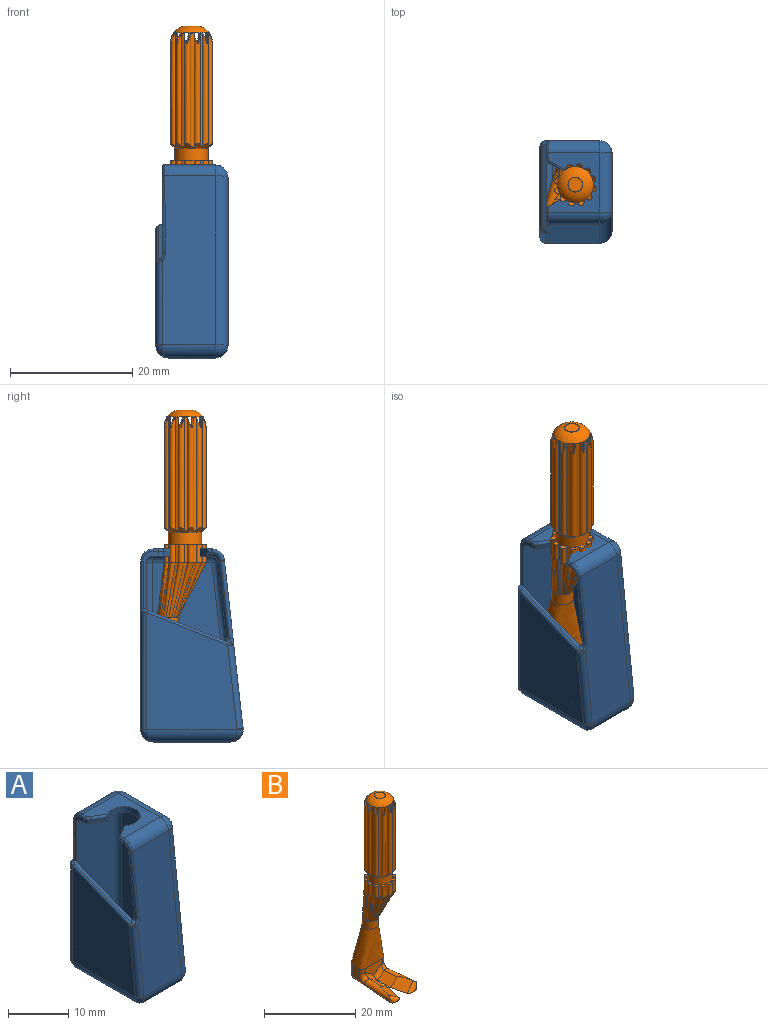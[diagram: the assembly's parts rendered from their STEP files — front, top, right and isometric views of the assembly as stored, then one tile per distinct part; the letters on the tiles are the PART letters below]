
ASSEMBLY  parts=2 mates=1
PART A: 136 faces, bbox 12x17.1x37.6 mm
  f0: plane 12.76x7.8mm, normal (0,0,-1), area 78.4mm2, adj f23,f27,f28,f29,f74,f75,f76,f77
  f1: plane 9.68x8.4mm, normal (0,0,1), area 45.1mm2, adj f14,f15,f17,f18,f19,f55,f56,f57
  f2: plane 9.71x8.6mm, normal (0,0,-1), area 44.8mm2, adj f3,f14,f15,f16,f41,f45,f48,f50
  f3: plane 9.56x2.48mm, normal (-1,0,0), area 5.7mm2, adj f2,f7,f12,f41,f51,f57,f58,f59
  f4: plane 27.72x8.92mm, normal (0,-0.99,0.11), area 237.7mm2, adj f17,f22,f27,f30,f66,f67,f68,f70
  f5: plane 12.87x7.6mm, normal (0,0,1), area 97.8mm2, adj f35,f36,f38,f39
  f6: plane 27.15x8.75mm, normal (0,0.99,-0.12), area 221mm2, adj f11,f38,f44,f47,f48,f52
  f7: plane 27x8.6mm, normal (0,-1,0), area 232.2mm2, adj f3,f11,f35,f40,f41
  f8: plane 27.6x8.8mm, normal (0,1,0), area 239.6mm2, adj f19,f24,f28,f33,f59,f60
  f9: plane 27x12.87mm, normal (-1,0,0), area 304.8mm2, adj f39,f40,f44,f45
  f10: plane 27.6x12.76mm, normal (1,0,0), area 309.6mm2, adj f18,f22,f23,f24
  f11: plane 19.27x14.89mm, normal (1,0,0), area 231.2mm2, adj f6,f7,f12,f36,f38,f52
  f12: plane 14.18x5.68mm, normal (0,-0.37,0.93), area 8.7mm2, adj f3,f11,f52,f61,f62,f63
  f13: plane 19.17x14.76mm, normal (-1,0,0), area 229.1mm2, adj f29,f30,f31,f33,f62
  f14: cylinder r=2.7mm len=5.4mm, axis (0,0,1), area 14.3mm2, adj f1,f2,f54,f55,f73
  f15: plane 2.88x1.8mm, normal (-0.52,0.86,0), area 3.5mm2, adj f1,f2,f50,f69,f73
  f16: plane 2.26x1.36mm, normal (-0.52,-0.86,0), area 2.1mm2, adj f2,f51,f54,f55
  f17: cylinder r=2mm len=8.37mm, axis (-1,0,0), area 24.4mm2, adj f1,f4,f20,f72
  f18: cylinder r=2mm len=9.68mm, axis (0,1,0), area 30.4mm2, adj f1,f10,f20,f21
  f19: cylinder r=2mm len=8.4mm, axis (1,0,0), area 26.4mm2, adj f1,f8,f21,f58
  f20: sphere r=2mm, area 5.8mm2, adj f17,f18,f22
  f21: sphere r=2mm, area 6.3mm2, adj f18,f19,f24
  f22: cylinder r=2mm len=27.82mm, axis (0,0.11,0.99), area 87.2mm2, adj f4,f10,f20,f25
  f23: cylinder r=2mm len=12.76mm, axis (0,-1,0), area 40.1mm2, adj f0,f10,f25,f26
  f24: cylinder r=2mm len=27.6mm, axis (0,0,-1), area 86.7mm2, adj f8,f10,f21,f26
  f25: sphere r=2mm, area 6.7mm2, adj f22,f23,f27
  f26: sphere r=2mm, area 6.3mm2, adj f23,f24,f28
  f27: cylinder r=2mm len=8.8mm, axis (1,0,0), area 28.5mm2, adj f0,f4,f25,f31,f32
  f28: cylinder r=2mm len=8.8mm, axis (-1,0,0), area 26.1mm2, adj f0,f8,f26,f34
  f29: cylinder r=2mm len=14.76mm, axis (0,-1,0), area 43.2mm2, adj f0,f13,f32,f34
  f30: cylinder r=1mm len=13.87mm, axis (0,0.11,0.99), area 21.5mm2, adj f4,f13,f31,f63,f64,f65
  f31: torus R=1mm, axis (-1,0,0), area 0.3mm2, adj f13,f27,f30,f32
  f32: bspline ~2.1x2mm, area 2.2mm2, adj f27,f29,f31
  f33: cylinder r=1mm len=19.41mm, axis (0,0,-1), area 30.3mm2, adj f8,f13,f34,f61
  f34: bspline ~2.39x2mm, area 2.2mm2, adj f28,f29,f33
  f35: cylinder r=1mm len=8.6mm, axis (1,0,0), area 12.7mm2, adj f5,f7,f36,f37
  f36: cylinder r=1mm len=14.87mm, axis (0,1,0), area 21.8mm2, adj f5,f11,f35,f38
  f37: sphere r=1mm, area 1mm2, adj f35,f39,f40
  f38: cylinder r=1mm len=8.6mm, axis (1,0,0), area 13.9mm2, adj f5,f6,f11,f36,f42
  f39: cylinder r=1mm len=12.87mm, axis (0,1,0), area 20.2mm2, adj f5,f9,f37,f42
  f40: cylinder r=1mm len=27mm, axis (0,0,1), area 42.4mm2, adj f7,f9,f37,f43
  f41: cylinder r=1mm len=8.6mm, axis (-1,0,0), area 13.5mm2, adj f2,f3,f7,f43
  f42: sphere r=1mm, area 1.7mm2, adj f38,f39,f44
  f43: sphere r=1mm, area 1mm2, adj f40,f41,f45
  f44: cylinder r=1mm len=27.12mm, axis (0,-0.12,-0.99), area 42.7mm2, adj f6,f9,f42,f46
  f45: cylinder r=1mm len=9.71mm, axis (0,-1,0), area 15.3mm2, adj f2,f9,f43,f46
  f46: sphere r=1mm, area 1.5mm2, adj f44,f45,f48
  f47: cylinder r=1mm len=12.74mm, axis (0,0.12,0.99), area 12.9mm2, adj f6,f49,f52,f68
  f48: cylinder r=1mm len=7.6mm, axis (-1,0,0), area 11.1mm2, adj f2,f6,f46,f49
  f49: torus R=2mm, axis (1,0,0), area 2.2mm2, adj f47,f48,f50,f70,f71,f72
  f50: cylinder r=1mm len=1.15mm, axis (0,1,0), area 1.1mm2, adj f2,f15,f49,f69
  f51: cylinder r=1mm len=0.86mm, axis (0,0,1), area 0.8mm2, adj f2,f3,f16,f56
  f52: bspline ~1.77x1.5mm, area 0.9mm2, adj f6,f11,f12,f47,f53,f64,f67
  f53: cylinder r=0.5mm len=0.15mm, axis (0,-0.93,-0.37), area 0mm2, adj f52,f65,f66
  f54: cylinder r=0.4mm len=1.17mm, axis (0,0,1), area 0.5mm2, adj f2,f14,f16,f55
  f55: cylinder r=0.4mm len=2.84mm, axis (0.86,-0.52,0), area 1.8mm2, adj f1,f14,f16,f54,f56
  f56: torus R=0.6mm, axis (0,0,1), area 0.6mm2, adj f1,f51,f55,f57
  f57: cylinder r=0.4mm len=0.87mm, axis (0,-1,0), area 0.5mm2, adj f1,f3,f56,f58
  f58: torus R=1.6mm, axis (1,0,0), area 1.8mm2, adj f3,f19,f57,f59
  f59: cylinder r=0.4mm len=8.19mm, axis (0,0,1), area 5mm2, adj f3,f8,f58,f60
  f60: cylinder r=0.4mm len=0.4mm, axis (-1,0,0), area 0.1mm2, adj f8,f59,f61
  f61: bspline ~1.15x1mm, area 1mm2, adj f3,f12,f33,f60,f62
  f62: cylinder r=0.4mm len=13.36mm, axis (0,-0.93,-0.37), area 8.9mm2, adj f12,f13,f61,f63
  f63: bspline ~0.61x0.51mm, area 0.3mm2, adj f12,f30,f62,f64
  f64: bspline ~0.58x0.57mm, area 0.2mm2, adj f30,f52,f63,f65
  f65: bspline ~0.66x0.42mm, area 0.1mm2, adj f30,f53,f64,f66
  f66: bspline ~0.28x0.27mm, area 0mm2, adj f4,f53,f65,f67
  f67: bspline ~1.3x0.83mm, area 0.7mm2, adj f4,f52,f66,f68
  f68: bspline ~33.52x4.28mm, area 10.7mm2, adj f4,f47,f67,f70
  f69: cylinder r=0.4mm len=0.81mm, axis (0,1,0), area 0.5mm2, adj f1,f15,f50,f71
  f70: bspline ~0.71x0.66mm, area 0.1mm2, adj f4,f49,f68,f72
  f71: bspline ~0.57x0.54mm, area 0.1mm2, adj f1,f49,f69,f72
  f72: bspline ~2.28x2.13mm, area 2mm2, adj f17,f49,f70,f71
  f73: cylinder r=0.4mm len=1.2mm, axis (0,0,1), area 0.6mm2, adj f1,f2,f14,f15
  f74: plane 0.6x0.43mm, normal (-1,0,0), area 0.3mm2, adj f0,f75,f82,f83
  f75: plane 3.85x0.6mm, normal (0,1,0), area 2.3mm2, adj f0,f74,f76,f83
  f76: plane 0.6x0.37mm, normal (1,0,0), area 0.2mm2, adj f0,f75,f77,f83
  f77: plane 1.02x0.79mm, normal (0.79,-0.61,0), area 0.8mm2, adj f0,f76,f78,f83
  f78: plane 0.6x0.3mm, normal (-0.61,-0.79,0), area 0.2mm2, adj f0,f77,f79,f83
  f79: extruded ~0.63x0.6mm, area 0.5mm2, adj f0,f78,f80,f83
  f80: extruded ~0.6x0.12mm, area 0.1mm2, adj f0,f79,f81,f83
  f81: extruded ~0.65x0.6mm, area 0.4mm2, adj f0,f80,f82,f83
  f82: plane 2.75x0.6mm, normal (0,-1,0), area 1.6mm2, adj f0,f74,f81,f83
  f83: plane 3.85x1.39mm, normal (0,0,-1), area 2mm2, adj f74,f75,f76,f77,f78,f79,f80,f81
  f84: extruded ~1.22x0.6mm, area 0.8mm2, adj f85,f99,f100,f134
  f85: extruded ~1.22x0.6mm, area 0.7mm2, adj f84,f86,f100,f134
  f86: extruded ~0.63x0.6mm, area 0.5mm2, adj f85,f87,f100,f134
  f87: extruded ~0.63x0.6mm, area 0.5mm2, adj f86,f88,f100,f134
  f88: extruded ~1.22x0.6mm, area 0.7mm2, adj f87,f89,f100,f134
  f89: extruded ~1.22x0.6mm, area 0.7mm2, adj f88,f90,f100,f134
  f90: extruded ~0.63x0.6mm, area 0.5mm2, adj f89,f99,f100,f134
  f91: extruded ~1.49x0.6mm, area 0.9mm2, adj f0,f92,f98,f100
  f92: extruded ~1.47x0.6mm, area 0.9mm2, adj f0,f91,f93,f100
  f93: extruded ~0.95x0.6mm, area 0.7mm2, adj f0,f92,f94,f100
  f94: extruded ~0.96x0.6mm, area 0.7mm2, adj f0,f93,f95,f100
  f95: extruded ~1.49x0.6mm, area 0.9mm2, adj f0,f94,f96,f100
  f96: extruded ~1.48x0.6mm, area 0.9mm2, adj f0,f95,f97,f100
  f97: extruded ~0.95x0.6mm, area 0.7mm2, adj f0,f96,f98,f100
  f98: extruded ~0.96x0.6mm, area 0.7mm2, adj f0,f91,f97,f100
  f99: extruded ~0.63x0.6mm, area 0.5mm2, adj f84,f90,f100,f134
  f100: plane 3.97x2.55mm, normal (0,0,-1), area 3.9mm2, adj f84,f85,f86,f87,f88,f89,f90,f91
  f101: extruded ~1.22x0.6mm, area 0.8mm2, adj f102,f116,f117,f135
  f102: extruded ~1.22x0.6mm, area 0.7mm2, adj f101,f103,f117,f135
  f103: extruded ~0.63x0.6mm, area 0.5mm2, adj f102,f104,f117,f135
  f104: extruded ~0.63x0.6mm, area 0.5mm2, adj f103,f105,f117,f135
  f105: extruded ~1.22x0.6mm, area 0.7mm2, adj f104,f106,f117,f135
  f106: extruded ~1.22x0.6mm, area 0.7mm2, adj f105,f107,f117,f135
  f107: extruded ~0.63x0.6mm, area 0.5mm2, adj f106,f116,f117,f135
  f108: extruded ~1.49x0.6mm, area 0.9mm2, adj f0,f109,f115,f117
  f109: extruded ~1.47x0.6mm, area 0.9mm2, adj f0,f108,f110,f117
  f110: extruded ~0.95x0.6mm, area 0.7mm2, adj f0,f109,f111,f117
  f111: extruded ~0.96x0.6mm, area 0.7mm2, adj f0,f110,f112,f117
  f112: extruded ~1.49x0.6mm, area 0.9mm2, adj f0,f111,f113,f117
  f113: extruded ~1.48x0.6mm, area 0.9mm2, adj f0,f112,f114,f117
  f114: extruded ~0.95x0.6mm, area 0.7mm2, adj f0,f113,f115,f117
  f115: extruded ~0.96x0.6mm, area 0.7mm2, adj f0,f108,f114,f117
  f116: extruded ~0.63x0.6mm, area 0.5mm2, adj f101,f107,f117,f135
  f117: plane 3.97x2.55mm, normal (0,0,-1), area 3.9mm2, adj f101,f102,f103,f104,f105,f106,f107,f108
  f118: extruded ~0.97x0.6mm, area 0.6mm2, adj f0,f119,f132,f133
  f119: extruded ~0.73x0.6mm, area 0.5mm2, adj f0,f118,f120,f133
  f120: plane 0.6x0.39mm, normal (0,1,0), area 0.2mm2, adj f0,f119,f121,f133
  f121: extruded ~0.74x0.6mm, area 0.5mm2, adj f0,f120,f122,f133
  f122: extruded ~0.64x0.6mm, area 0.4mm2, adj f0,f121,f123,f133
  f123: extruded ~0.82x0.6mm, area 0.5mm2, adj f0,f122,f124,f133
  f124: extruded ~1.12x0.88mm, area 1mm2, adj f0,f123,f125,f133
  f125: extruded ~0.6x0.3mm, area 0.2mm2, adj f0,f124,f126,f133
  f126: extruded ~0.6x0.32mm, area 0.2mm2, adj f0,f125,f127,f133
  f127: plane 0.6x0.37mm, normal (-0.34,0.94,0), area 0.2mm2, adj f0,f126,f128,f133
  f128: extruded ~0.6x0.33mm, area 0.2mm2, adj f0,f127,f129,f133
  f129: extruded ~0.6x0.42mm, area 0.3mm2, adj f0,f128,f130,f133
  f130: extruded ~1x0.6mm, area 0.7mm2, adj f0,f129,f131,f133
  f131: extruded ~1.12x0.6mm, area 0.7mm2, adj f0,f130,f132,f133
  f132: extruded ~1.09x0.6mm, area 0.7mm2, adj f0,f118,f131,f133
  f133: plane 3x2.09mm, normal (0,0,-1), area 2.2mm2, adj f118,f119,f120,f121,f122,f123,f124,f125
  f134: plane 3.21x1.66mm, normal (0,0,-1), area 4.5mm2, adj f84,f85,f86,f87,f88,f89,f90,f99
  f135: plane 3.21x1.66mm, normal (0,0,-1), area 4.5mm2, adj f101,f102,f103,f104,f105,f106,f107,f116
PART B: 140 faces, bbox 9.3x13.9x50.9 mm
  f0: plane 2.34x2.34mm, normal (0,0,1), area 4.3mm2, adj f1
  f1: torus R=1.17mm, axis (0,0,-1), area 0.3mm2, adj f0
  f2: plane 5.03x3.02mm, normal (0,1,0), area 12.5mm2, adj f3,f11,f12,f13,f14,f15,f16,f17
  f3: plane 0.8x0.18mm, normal (-1,0,0), area 0.1mm2, adj f2,f4,f11,f139
  f4: plane 3.76x1.81mm, normal (0,1,0), area 2mm2, adj f3,f5,f6,f7,f8,f9,f10,f11
  f5: extruded ~0.97x0.85mm, area 1.1mm2, adj f4,f6,f59,f138
  f6: extruded ~0.67x0.49mm, area 0.3mm2, adj f4,f5,f7,f59
  f7: plane 0.72x0.32mm, normal (0.95,0,0.31), area 0.2mm2, adj f4,f6,f8,f59
  f8: extruded ~0.72x0.39mm, area 0.3mm2, adj f4,f7,f9,f59
  f9: extruded ~0.73x0.33mm, area 0.3mm2, adj f4,f8,f10,f59
  f10: extruded ~0.8x0.48mm, area 0.4mm2, adj f4,f9,f18,f59
  f11: plane 0.8x0.47mm, normal (0,0,1), area 0.4mm2, adj f2,f3,f4,f12
  f12: plane 2.32x0.8mm, normal (-1,0,0), area 1.9mm2, adj f2,f4,f11,f13
  f13: plane 0.8x0.4mm, normal (0,0,1), area 0.3mm2, adj f2,f4,f12,f14
  f14: plane 2.32x0.8mm, normal (1,0,0), area 1.9mm2, adj f2,f4,f13,f15
  f15: plane 0.8x0.67mm, normal (0,0,1), area 0.5mm2, adj f2,f4,f14,f16
  f16: plane 0.8x0.31mm, normal (1,0,0), area 0.2mm2, adj f2,f4,f15,f17
  f17: plane 0.8x0.67mm, normal (0,0,-1), area 0.5mm2, adj f2,f4,f16,f18
  f18: plane 0.8x0.17mm, normal (1,0,0), area 0.1mm2, adj f2,f4,f10,f17,f59
  f19: cylinder r=1mm len=3mm, axis (0,0,1), area 4.5mm2, adj f2,f20,f45,f59
  f20: plane 3x2.85mm, normal (-1,0.08,0), area 6.5mm2, adj f19,f21,f43,f44,f59
  f21: cylinder r=1mm len=12.57mm, axis (-0.08,-1,0), area 17.9mm2, adj f20,f22,f40,f41,f42,f44,f45
  f22: plane 0.39x0.27mm, normal (-0.25,-0.97,0), area 0.1mm2, adj f21,f23,f40,f42
  f23: cylinder r=1mm len=3.37mm, axis (0.81,-0.21,-0.55), area 3.7mm2, adj f22,f24,f40,f41,f42
  f24: plane 4.37x3.6mm, normal (0.54,-0.14,0.83), area 12.7mm2, adj f23,f25,f40,f41
  f25: plane 4.02x2.46mm, normal (0.55,-0.02,0.83), area 10.5mm2, adj f24,f26,f40,f41
  f26: cylinder r=1mm len=3.75mm, axis (-0.83,0,0.55), area 4.3mm2, adj f25,f27,f39,f40,f44
  f27: cylinder r=1mm len=3.75mm, axis (0.83,0,0.55), area 4.3mm2, adj f26,f28,f38,f39,f40
  f28: bspline ~2.3x2.06mm, area 4.3mm2, adj f27,f29,f35,f36,f37
  f29: cylinder r=1mm len=12.57mm, axis (-0.08,1,0), area 17.9mm2, adj f28,f30,f31,f34,f35,f37,f40
  f30: sphere r=1mm, area 1mm2, adj f29,f46,f47
  f31: plane 0.39x0.27mm, normal (0.25,-0.97,0), area 0.1mm2, adj f29,f32,f34,f40
  f32: cylinder r=1mm len=3.37mm, axis (0.81,0.21,0.55), area 3.7mm2, adj f31,f33,f34,f35,f40
  f33: plane 4.37x3.6mm, normal (-0.54,-0.14,0.83), area 12.7mm2, adj f32,f35,f38,f40
  f34: cylinder r=1mm len=1.48mm, axis (0,0,1), area 0.9mm2, adj f29,f31,f32,f35
  f35: cylinder r=1mm len=8.25mm, axis (0.08,-1,0.03), area 13mm2, adj f28,f29,f32,f33,f34,f38
  f36: cylinder r=1mm len=1.08mm, axis (0,0,1), area 1.8mm2, adj f28,f37,f39,f59
  f37: plane 3x2.85mm, normal (1,0.08,0), area 6.5mm2, adj f28,f29,f36,f47,f59
  f38: plane 4.02x2.46mm, normal (-0.55,-0.02,0.83), area 10.5mm2, adj f27,f33,f35,f40
  f39: plane 5.32x2.85mm, normal (0,-1,0), area 10.5mm2, adj f26,f27,f36,f43,f59
  f40: plane 12.68x6.95mm, normal (0,0,-1), area 66.6mm2, adj f21,f22,f23,f24,f25,f26,f27,f29
  f41: cylinder r=1mm len=8.25mm, axis (0.08,1,-0.03), area 13mm2, adj f21,f23,f24,f25,f42,f44
  f42: cylinder r=1mm len=1.48mm, axis (0,0,1), area 0.9mm2, adj f21,f22,f23,f41
  f43: cylinder r=1mm len=1.08mm, axis (0,0,1), area 1.8mm2, adj f20,f39,f44,f59
  f44: bspline ~2.3x2.07mm, area 4.3mm2, adj f20,f21,f26,f41,f43
  f45: sphere r=1mm, area 2.1mm2, adj f19,f21,f46
  f46: cylinder r=1mm len=5.02mm, axis (-1,0,0), area 7.9mm2, adj f2,f30,f40,f45
  f47: cylinder r=1mm len=3mm, axis (0,0,-1), area 4.5mm2, adj f2,f30,f37,f59
  f48: plane 0.8x0.27mm, normal (-0.79,0,0.61), area 0.3mm2, adj f2,f49,f51,f53
  f49: plane 0.94x0.81mm, normal (-0.61,0,-0.79), area 0.9mm2, adj f48,f50,f51,f59
  f50: plane 0.72x0.34mm, normal (0,0,-1), area 0.2mm2, adj f49,f51,f58,f59
  f51: plane 3.51x1.26mm, normal (0,1,0), area 1.7mm2, adj f48,f49,f50,f52,f53,f55,f56,f57
  f52: extruded ~0.78x0.11mm, area 0.1mm2, adj f51,f53,f54,f55
  f53: extruded ~0.8x0.57mm, area 0.6mm2, adj f2,f48,f51,f52,f54
  f54: bspline ~10x3.32mm, area 0mm2, adj f2,f52,f53,f55
  f55: extruded ~0.8x0.59mm, area 0.5mm2, adj f2,f51,f52,f54,f56
  f56: plane 2.5x0.8mm, normal (-1,0,0), area 2mm2, adj f2,f51,f55,f57
  f57: plane 0.8x0.39mm, normal (0,0,1), area 0.3mm2, adj f2,f51,f56,f58
  f58: plane 3.51x0.8mm, normal (1,0,0), area 2.8mm2, adj f2,f50,f51,f57,f59
  f59: bspline ~10x7.3mm, area 158.1mm2, adj f2,f5,f6,f7,f8,f9,f10,f18
  f60: cylinder r=1.78mm len=3.56mm, axis (0,0,-1), area 22.4mm2, adj f59,f61,f115,f116,f117,f118,f119,f120
  f61: bspline ~9x4.44mm, area 9.4mm2, adj f60,f62,f115,f137
  f62: cylinder r=0.5mm len=3mm, axis (0,0,-1), area 5mm2, adj f61,f63,f85,f114
  f63: cylinder r=3mm len=3mm, axis (0,0,-1), area 1.7mm2, adj f62,f64,f85,f137
  f64: cylinder r=0.5mm len=3mm, axis (0,0,-1), area 5mm2, adj f63,f65,f85,f136
  f65: cylinder r=3mm len=3mm, axis (0,0,-1), area 1.7mm2, adj f64,f66,f85,f135
  f66: cylinder r=0.5mm len=3mm, axis (0,0,-1), area 5mm2, adj f65,f67,f85,f134
  f67: cylinder r=3mm len=3mm, axis (0,0,-1), area 1.7mm2, adj f66,f68,f85,f133
  f68: cylinder r=0.5mm len=3mm, axis (0,0,-1), area 5mm2, adj f67,f69,f85,f132
  f69: cylinder r=3mm len=3mm, axis (0,0,-1), area 1.7mm2, adj f68,f70,f85,f131
  f70: cylinder r=0.5mm len=3mm, axis (0,0,-1), area 5mm2, adj f69,f71,f85,f130
  f71: cylinder r=3mm len=3mm, axis (0,0,-1), area 1.7mm2, adj f70,f72,f85,f129
  f72: cylinder r=0.5mm len=3mm, axis (0,0,-1), area 5mm2, adj f71,f73,f85,f128
  f73: cylinder r=3mm len=3mm, axis (0,0,-1), area 1.7mm2, adj f72,f74,f85,f127
  f74: cylinder r=0.5mm len=3mm, axis (0,0,-1), area 5mm2, adj f73,f75,f85,f126
  f75: cylinder r=3mm len=3mm, axis (0,0,-1), area 1.7mm2, adj f74,f76,f85,f125
  f76: cylinder r=0.5mm len=3mm, axis (0,0,-1), area 5mm2, adj f75,f77,f85,f124
  f77: cylinder r=3mm len=3mm, axis (0,0,-1), area 1.7mm2, adj f76,f78,f85,f123
  f78: cylinder r=0.5mm len=3mm, axis (0,0,-1), area 5mm2, adj f77,f79,f85,f122
  f79: cylinder r=3mm len=3mm, axis (0,0,-1), area 1.7mm2, adj f78,f80,f85,f121
  f80: cylinder r=0.5mm len=3mm, axis (0,0,-1), area 5mm2, adj f79,f81,f85,f120
  f81: cylinder r=3mm len=3mm, axis (0,0,-1), area 1.7mm2, adj f80,f82,f85,f119
  f82: cylinder r=0.5mm len=3mm, axis (0,0,-1), area 5mm2, adj f81,f83,f85,f118
  f83: cylinder r=3mm len=3mm, axis (0,0,-1), area 1.7mm2, adj f82,f84,f85,f117
  f84: cylinder r=0.5mm len=3mm, axis (0,0,-1), area 5mm2, adj f83,f85,f114,f116
  f85: plane 7x7mm, normal (0,0,1), area 9.4mm2, adj f62,f63,f64,f65,f66,f67,f68,f69
  f86: cylinder r=2.75mm len=5.5mm, axis (0,0,-1), area 34.6mm2, adj f85,f87
  f87: cone r=3.75mm half-angle=45deg, axis (0,0,1), area 13.3mm2, adj f86,f88,f91,f92,f93,f94,f95,f96
  f88: cylinder r=3mm len=18.56mm, axis (0,0,-1), area 10.6mm2, adj f87,f89,f91,f113
  f89: revolved ~6.9x6.9mm, area 18.7mm2, adj f88,f90,f91,f92,f93,f94,f95,f96
  f90: revolved ~5.92x5.92mm, area 57.8mm2, adj f89
  f91: cylinder r=0.5mm len=18.56mm, axis (0,0,-1), area 29.3mm2, adj f87,f88,f89,f92
  f92: cylinder r=3mm len=18.56mm, axis (0,0,-1), area 10.6mm2, adj f87,f89,f91,f93
  f93: cylinder r=0.5mm len=18.56mm, axis (0,0,-1), area 29.3mm2, adj f87,f89,f92,f94
  f94: cylinder r=3mm len=18.56mm, axis (0,0,-1), area 10.6mm2, adj f87,f89,f93,f95
  f95: cylinder r=0.5mm len=18.56mm, axis (0,0,-1), area 29.3mm2, adj f87,f89,f94,f96
  f96: cylinder r=3mm len=18.56mm, axis (0,0,-1), area 10.6mm2, adj f87,f89,f95,f97
  f97: cylinder r=0.5mm len=18.56mm, axis (0,0,-1), area 29.3mm2, adj f87,f89,f96,f98
  f98: cylinder r=3mm len=18.56mm, axis (0,0,-1), area 10.6mm2, adj f87,f89,f97,f99
  f99: cylinder r=0.5mm len=18.56mm, axis (0,0,-1), area 29.3mm2, adj f87,f89,f98,f100
  f100: cylinder r=3mm len=18.56mm, axis (0,0,-1), area 10.6mm2, adj f87,f89,f99,f101
  f101: cylinder r=0.5mm len=18.56mm, axis (0,0,-1), area 29.3mm2, adj f87,f89,f100,f102
  f102: cylinder r=3mm len=18.56mm, axis (0,0,-1), area 10.6mm2, adj f87,f89,f101,f103
  f103: cylinder r=0.5mm len=18.56mm, axis (0,0,-1), area 29.3mm2, adj f87,f89,f102,f104
  f104: cylinder r=3mm len=18.56mm, axis (0,0,-1), area 10.6mm2, adj f87,f89,f103,f105
  f105: cylinder r=0.5mm len=18.56mm, axis (0,0,-1), area 29.3mm2, adj f87,f89,f104,f106
  f106: cylinder r=3mm len=18.56mm, axis (0,0,-1), area 10.6mm2, adj f87,f89,f105,f107
  f107: cylinder r=0.5mm len=18.56mm, axis (0,0,-1), area 29.3mm2, adj f87,f89,f106,f108
  f108: cylinder r=3mm len=18.56mm, axis (0,0,-1), area 10.6mm2, adj f87,f89,f107,f109
  f109: cylinder r=0.5mm len=18.56mm, axis (0,0,-1), area 29.3mm2, adj f87,f89,f108,f110
  f110: cylinder r=3mm len=18.56mm, axis (0,0,-1), area 10.6mm2, adj f87,f89,f109,f111
  f111: cylinder r=0.5mm len=18.56mm, axis (0,0,-1), area 29.3mm2, adj f87,f89,f110,f112
  f112: cylinder r=3mm len=18.56mm, axis (0,0,-1), area 10.6mm2, adj f87,f89,f111,f113
  f113: cylinder r=0.5mm len=18.56mm, axis (0,0,-1), area 28.7mm2, adj f87,f88,f89,f112
  f114: cylinder r=3mm len=3mm, axis (0,0,-1), area 1.7mm2, adj f62,f84,f85,f115
  f115: bspline ~9x3.78mm, area 4.6mm2, adj f60,f61,f114,f116
  f116: bspline ~9x3.48mm, area 9.3mm2, adj f60,f84,f115,f117
  f117: bspline ~9x2.76mm, area 4.6mm2, adj f60,f83,f116,f118
  f118: bspline ~9x2.39mm, area 9.1mm2, adj f60,f82,f117,f119
  f119: bspline ~9x1.89mm, area 4.7mm2, adj f60,f81,f118,f120
  f120: bspline ~9x1.65mm, area 9.1mm2, adj f60,f80,f119,f121
  f121: bspline ~9x1.58mm, area 4.6mm2, adj f60,f79,f120,f122
  f122: bspline ~9x1.77mm, area 9mm2, adj f60,f78,f121,f123
  f123: bspline ~9x1.78mm, area 4.6mm2, adj f60,f77,f122,f124
  f124: bspline ~9x2.2mm, area 9.1mm2, adj f60,f76,f123,f125
  f125: bspline ~9x2.29mm, area 4.6mm2, adj f60,f75,f124,f126
  f126: bspline ~9x2.84mm, area 9.3mm2, adj f60,f74,f125,f127
  f127: bspline ~9x2.96mm, area 4.8mm2, adj f60,f73,f126,f128
  f128: bspline ~9x3.57mm, area 9.5mm2, adj f60,f72,f127,f129
  f129: bspline ~9x3.63mm, area 4.9mm2, adj f60,f71,f128,f130
  f130: bspline ~9x4.29mm, area 9.7mm2, adj f60,f70,f129,f131
  f131: bspline ~9x4.2mm, area 5mm2, adj f60,f69,f130,f132
  f132: bspline ~9x4.95mm, area 9.7mm2, adj f60,f68,f131,f133
  f133: bspline ~9x4.72mm, area 5mm2, adj f60,f67,f132,f134
  f134: bspline ~9x5.27mm, area 9.7mm2, adj f60,f66,f133,f135
  f135: bspline ~9x4.91mm, area 4.8mm2, adj f60,f65,f134,f136
  f136: bspline ~9x5.08mm, area 9.5mm2, adj f60,f64,f135,f137
  f137: bspline ~9x4.56mm, area 4.6mm2, adj f60,f61,f63,f136
  f138: plane 0.8x0.15mm, normal (-1,0,0), area 0.1mm2, adj f2,f4,f5,f139
  f139: plane 0.8x0.47mm, normal (-0.29,0,-0.96), area 0.4mm2, adj f2,f3,f4,f138
PLACE A at identity fixed
PLACE B rot(axis=(0,0,-1),12deg) t=(0.29,-0.03,2.34)mm
MATE cylindrical B.f1 <-> A.f14  axis (0,0,1) through (0,-1.38,52.34)mm
